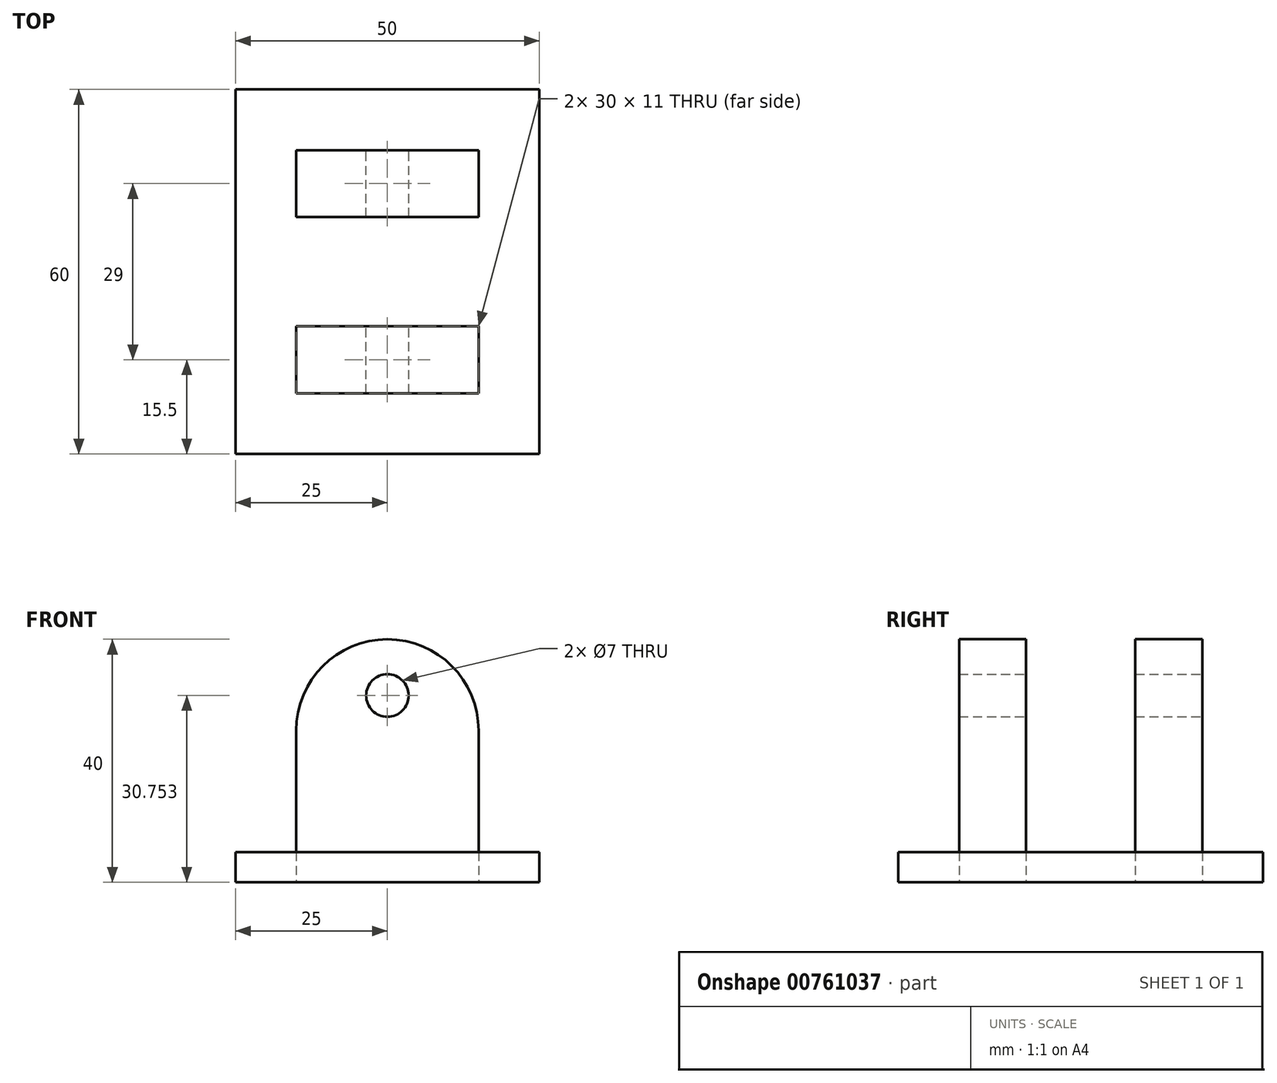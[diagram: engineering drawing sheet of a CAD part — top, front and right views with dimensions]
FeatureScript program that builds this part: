
annotation { "Feature Type Name" : "Feature", "Feature Type Description" : "" }
export const myFeature = defineFeature(function(context is Context, id is Id, definition is map)
    precondition{}
    {
        {
            var Q0;
            Q0=qCreatedBy(makeId("Top.planeOp"),FACE);
            var sketch = newSketch(context, id + "F0", { "sketchPlane" : qUnion([Q0])});
            skLineSegment(sketch, "E0.bottom", {"start": v(-25, 30) * mm, "end": v(25, 30) * mm});
            skLineSegment(sketch, "E0.top", {"start": v(-25, -30) * mm, "end": v(25, -30) * mm});
            skLineSegment(sketch, "E0.left", {"start": v(-25, 30) * mm, "end": v(-25, -30) * mm});
            skLineSegment(sketch, "E0.right", {"start": v(25, 30) * mm, "end": v(25, -30) * mm});
            skPoint(sketch, "E0.middle", {"position": v(0, 0) * mm});
            skLineSegment(sketch, "E1.bottom", {"start": v(-15, 20) * mm, "end": v(15, 20) * mm});
            skLineSegment(sketch, "E1.top", {"start": v(-15, 9) * mm, "end": v(15, 9) * mm});
            skLineSegment(sketch, "E1.left", {"start": v(-15, 20) * mm, "end": v(-15, 9) * mm});
            skLineSegment(sketch, "E1.right", {"start": v(15, 20) * mm, "end": v(15, 9) * mm});
            skLineSegment(sketch, "E2.bottom", {"start": v(-15, -9) * mm, "end": v(15, -9) * mm});
            skLineSegment(sketch, "E2.top", {"start": v(-15, -20) * mm, "end": v(15, -20) * mm});
            skLineSegment(sketch, "E2.left", {"start": v(-15, -9) * mm, "end": v(-15, -20) * mm});
            skLineSegment(sketch, "E2.right", {"start": v(15, -9) * mm, "end": v(15, -20) * mm});
            skSolve(sketch);
        }
        {
            var Q0;
            Q0=makeQuery(id+"F0.imprint","IMPRINT",FACE,{"disambiguationData":[TD([[makeQuery(id+"F0.imprint","IMPRINT",EDGE,{"derivedFrom":sQuery(id+"F0.wireOp",EDGE,"E1.bottom")}),-1.0]])]});
            var Q1;
            Q1=makeQuery(id+"F0.imprint","IMPRINT",FACE,{"disambiguationData":[TD([[makeQuery(id+"F0.imprint","IMPRINT",EDGE,{"derivedFrom":sQuery(id+"F0.wireOp",EDGE,"E2.bottom")}),-1.0]])]});
            extrude(context, id + "F1", {"entities" : qUnion([Q0, Q1]), "depth" : 40 * mm, "offsetDistance" : 25 * mm});
        }
        {
            var Q0;
            Q0 = qSketchRegion(id + "F0", true);
            extrude(context, id + "F2", {"entities" : qUnion([Q0]), "depth" : 5 * mm, "offsetDistance" : 25 * mm});
        }
        {
            var Q0;
            Q0=makeQuery(id+"F1.opExtrude","CAP_EDGE",EDGE,{"disambiguationData":[OSD([sQuery(id+"F0.wireOp",EDGE,"E2.right")])],"isStart":false});
            var Q1;
            Q1=makeQuery(id+"F1.opExtrude","CAP_EDGE",EDGE,{"disambiguationData":[OSD([sQuery(id+"F0.wireOp",EDGE,"E2.left")])],"isStart":false});
            var Q2;
            Q2=makeQuery(id+"F1.opExtrude","CAP_EDGE",EDGE,{"disambiguationData":[OSD([sQuery(id+"F0.wireOp",EDGE,"E1.right")])],"isStart":false});
            var Q3;
            Q3=makeQuery(id+"F1.opExtrude","CAP_EDGE",EDGE,{"disambiguationData":[OSD([sQuery(id+"F0.wireOp",EDGE,"E1.left")])],"isStart":false});
            fillet(context, id + "F3", {"entities" : qUnion([Q0, Q1, Q2, Q3]), "radius" : 15 * mm, "tangentPropagation" : true, "allowEdgeOverflow" : false});
        }
        {
            var Q0;
            Q0=makeQuery(id+"F1.opExtrude","SWEPT_FACE",FACE,{"disambiguationData":[OSD([sQuery(id+"F0.wireOp",EDGE,"E1.bottom")])]});
            var sketch = newSketch(context, id + "F4", { "sketchPlane" : qUnion([Q0])});
            skCircle(sketch, "E3", {"center": v(0, 30.75) * mm, "radius": 2.5 * mm});
            skPoint(sketch, "E3.centerSnap0", {"position": v(0, 40) * mm});
            skSolve(sketch);
        }
        {
            var Q0;
            Q0=sQuery(id+"F4.wireOp",VERTEX,"E3.center");
            var Q1;
            Q1=makeQuery(id+"F1.opExtrude","SWEPT_BODY",BODY,{"disambiguationData":[OSD([sQuery(id+"F0.wireOp",EDGE,"E1.bottom"),sQuery(id+"F0.wireOp",EDGE,"E1.top"),sQuery(id+"F0.wireOp",EDGE,"E1.left"),sQuery(id+"F0.wireOp",EDGE,"E1.right")])]});
            var Q2;
            Q2=makeQuery(id+"F1.opExtrude","SWEPT_BODY",BODY,{"disambiguationData":[OSD([sQuery(id+"F0.wireOp",EDGE,"E2.bottom"),sQuery(id+"F0.wireOp",EDGE,"E2.top"),sQuery(id+"F0.wireOp",EDGE,"E2.left"),sQuery(id+"F0.wireOp",EDGE,"E2.right")])]});
            hole(context, id + "F5", {"style" : HoleStyle.SIMPLE, "endStyle" : HoleEndStyle.THROUGH, "holeDiameter" : 7 * mm, "majorDiameter" : 5 * mm, "isTappedThrough" : true, "tappedDepth" : 12 * mm, "tapClearance" : 3, "locations" : qUnion([Q0]), "scope" : qUnion([Q1, Q2])});
        }
    });
